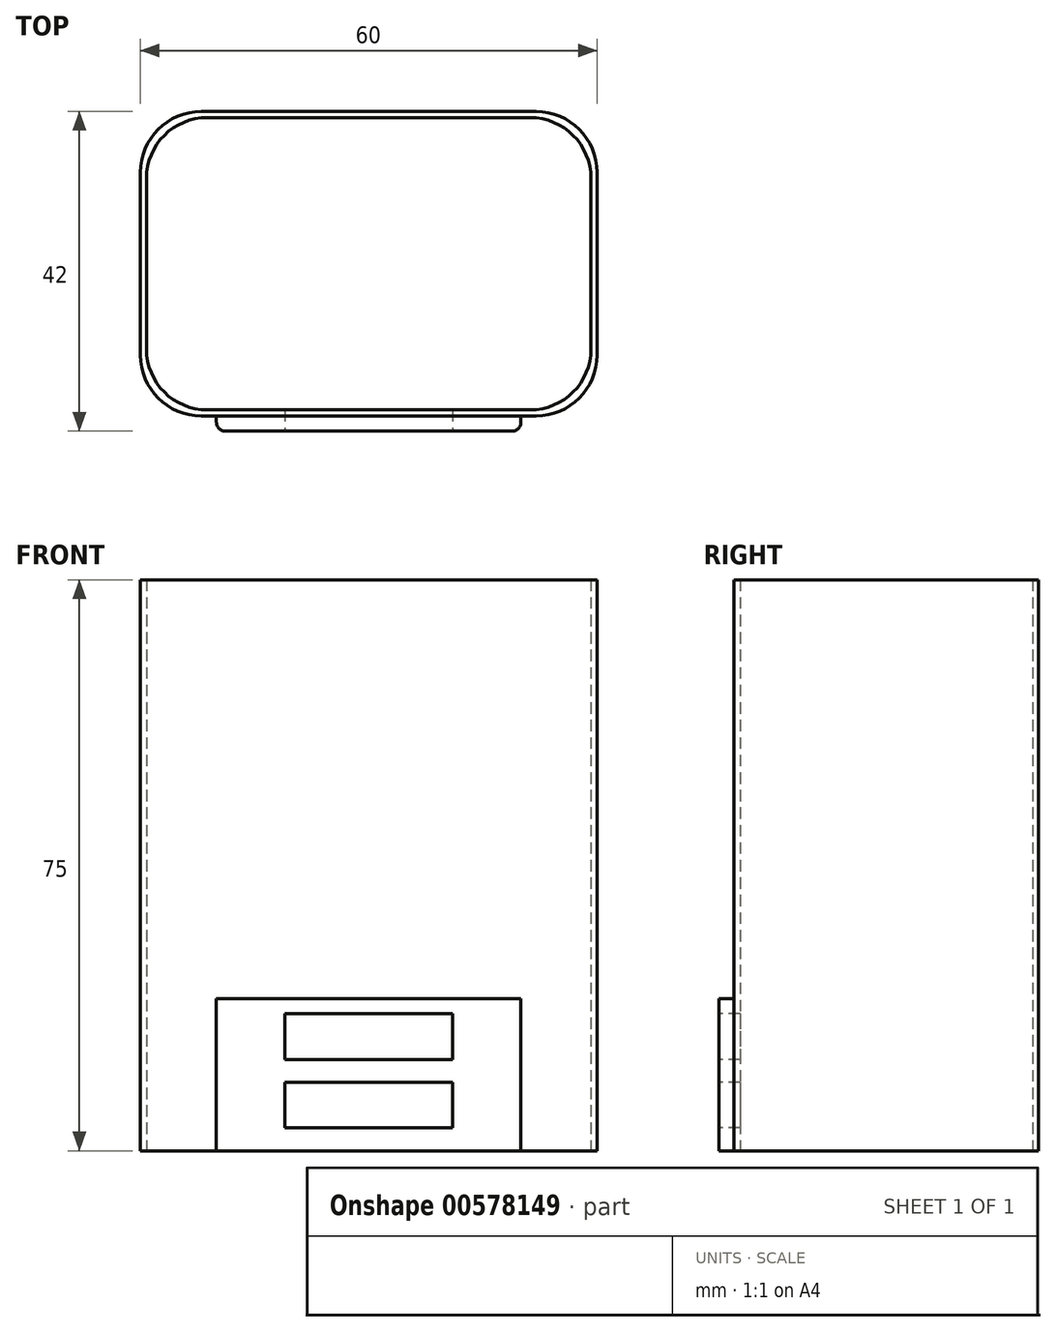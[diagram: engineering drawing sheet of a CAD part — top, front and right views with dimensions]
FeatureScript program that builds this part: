
annotation { "Feature Type Name" : "Feature", "Feature Type Description" : "" }
export const myFeature = defineFeature(function(context is Context, id is Id, definition is map)
    precondition{}
    {
        {
            var Q0;
            Q0=qCreatedBy(makeId("Top.planeOp"),FACE);
            var sketch = newSketch(context, id + "F0", { "sketchPlane" : qUnion([Q0])});
            skLineSegment(sketch, "E0.bottom", {"start": v(30, -33.61) * mm, "end": v(-30, -33.61) * mm});
            skPoint(sketch, "E0.middle", {"position": v(0, 0) * mm});
            skLineSegment(sketch, "E1.bottom", {"start": v(-30, -33.61) * mm, "end": v(30, -33.61) * mm});
            skLineSegment(sketch, "E1.top", {"start": v(-20, -35.61) * mm, "end": v(20, -35.61) * mm});
            skLineSegment(sketch, "E2.top", {"start": v(-10, -41.75) * mm, "end": v(10, -41.75) * mm});
            skLineSegment(sketch, "E3.top", {"start": v(-10, -47.65) * mm, "end": v(10, -47.65) * mm});
            skPoint(sketch, "E4.start.orphan", {"position": v(30, -38.68) * mm});
            skPoint(sketch, "E5.start.orphan", {"position": v(-30, -38.68) * mm});
            skLineSegment(sketch, "E6", {"start": v(-10, -47.65) * mm, "end": v(-10, -35.61) * mm});
            skLineSegment(sketch, "E7", {"start": v(10, -47.65) * mm, "end": v(10, -35.61) * mm});
            skPoint(sketch, "E8.start.orphan", {"position": v(10, -51.4) * mm});
            skPoint(sketch, "E9.start.orphan", {"position": v(-10, -50.9) * mm});
            skPoint(sketch, "E10.orphan", {"position": v(-30, -41.75) * mm});
            skPoint(sketch, "E11.orphan", {"position": v(30, -41.75) * mm});
            skLineSegment(sketch, "E12.top", {"start": v(-30, 6.39) * mm, "end": v(30, 6.39) * mm});
            skLineSegment(sketch, "E12.left", {"start": v(-30, -33.61) * mm, "end": v(-30, 6.39) * mm});
            skLineSegment(sketch, "E12.right", {"start": v(30, -33.61) * mm, "end": v(30, 6.39) * mm});
            skLineSegment(sketch, "E13", {"start": v(20, -35.61) * mm, "end": v(20, -33.61) * mm});
            skLineSegment(sketch, "E14", {"start": v(-20, -35.61) * mm, "end": v(-20, -33.61) * mm});
            skPoint(sketch, "E15.orphan", {"position": v(-30, -35.61) * mm});
            skPoint(sketch, "E16.orphan", {"position": v(30, -35.61) * mm});
            skLineSegment(sketch, "E17.bottom", {"start": v(-29.2, -32.81) * mm, "end": v(29.2, -32.81) * mm});
            skLineSegment(sketch, "E17.top", {"start": v(-29.2, 5.59) * mm, "end": v(29.2, 5.59) * mm});
            skLineSegment(sketch, "E17.left", {"start": v(-29.2, -32.81) * mm, "end": v(-29.2, 5.59) * mm});
            skLineSegment(sketch, "E17.right", {"start": v(29.2, -32.81) * mm, "end": v(29.2, 5.59) * mm});
            skPoint(sketch, "E17.middle", {"position": v(0, -13.61) * mm});
            skSolve(sketch);
        }
        {
            var Q0;
            {var subQ0=sQuery(id+"F0.wireOp",EDGE,"E13");Q0=makeQuery(id+"F0.imprint","IMPRINT",FACE,{"disambiguationData":[TD([[makeQuery(id+"F0.imprint","IMPRINT",EDGE,{"derivedFrom":subQ0}),1.0]])]});}
            extrude(context, id + "F1", {"entities" : qUnion([Q0]), "depth" : 20 * mm, "offsetDistance" : 25 * mm});
        }
        {
            var Q0;
            Q0=makeQuery(id+"F0.imprint","IMPRINT",FACE,{"disambiguationData":[TD([[makeQuery(id+"F0.imprint","IMPRINT",EDGE,{"derivedFrom":sQuery(id+"F0.wireOp",EDGE,"E12.top")}),-1.0]])]});
            extrude(context, id + "F2", {"entities" : qUnion([Q0]), "operationType" : NewBodyOperationType.ADD, "depth" : 75 * mm, "offsetDistance" : 25 * mm});
        }
        {
            var Q0;
            Q0=makeQuery(id+"F1.opExtrude","SWEPT_EDGE",EDGE,{"disambiguationData":[OSD([sQuery(id+"F0.wireOp",EDGE,"E3.top"),sQuery(id+"F0.wireOp",EDGE,"E7")])]});
            var Q1;
            Q1=makeQuery(id+"F1.opExtrude","SWEPT_EDGE",EDGE,{"disambiguationData":[OSD([sQuery(id+"F0.wireOp",EDGE,"E3.top"),sQuery(id+"F0.wireOp",EDGE,"E6")])]});
            var Q2;
            Q2=makeQuery(id+"F1.opExtrude","SWEPT_EDGE",EDGE,{"disambiguationData":[OSD([sQuery(id+"F0.wireOp",EDGE,"E1.top"),sQuery(id+"F0.wireOp",EDGE,"E13")])]});
            var Q3;
            Q3=makeQuery(id+"F1.opExtrude","SWEPT_EDGE",EDGE,{"disambiguationData":[OSD([sQuery(id+"F0.wireOp",EDGE,"E1.top"),sQuery(id+"F0.wireOp",EDGE,"E14")])]});
            var Q4;
            Q4=makeQuery(id+"F1.opExtrude","CAP_FACE",FACE,{"disambiguationData":[OSD([sQuery(id+"F0.wireOp",EDGE,"E2.top"),sQuery(id+"F0.wireOp",EDGE,"E3.top"),sQuery(id+"F0.wireOp",EDGE,"E6"),sQuery(id+"F0.wireOp",EDGE,"E7")])],"isStart":false});
            var Q5;
            Q5=makeQuery(id+"F1.opExtrude","CAP_EDGE",EDGE,{"disambiguationData":[OSD([sQuery(id+"F0.wireOp",EDGE,"E3.top")])],"isStart":true});
            fillet(context, id + "F3", {"entities" : qUnion([Q0, Q1, Q2, Q3, Q4, Q5]), "radius" : 1.2 * mm, "tangentPropagation" : true, "allowEdgeOverflow" : false});
        }
        {
            var Q0;
            Q0=makeQuery(id+"F2.opExtrude","SWEPT_EDGE",EDGE,{"disambiguationData":[OSD([sQuery(id+"F0.wireOp",EDGE,"E17.top"),sQuery(id+"F0.wireOp",EDGE,"E17.right")])]});
            var Q1;
            Q1=makeQuery(id+"F2.opExtrude","SWEPT_EDGE",EDGE,{"disambiguationData":[OSD([sQuery(id+"F0.wireOp",EDGE,"E17.bottom"),sQuery(id+"F0.wireOp",EDGE,"E17.right")])]});
            var Q2;
            Q2=makeQuery(id+"F2.opExtrude","SWEPT_EDGE",EDGE,{"disambiguationData":[OSD([sQuery(id+"F0.wireOp",EDGE,"E17.bottom"),sQuery(id+"F0.wireOp",EDGE,"E17.left")])]});
            var Q3;
            Q3=makeQuery(id+"F2.opExtrude","SWEPT_EDGE",EDGE,{"disambiguationData":[OSD([sQuery(id+"F0.wireOp",EDGE,"E17.top"),sQuery(id+"F0.wireOp",EDGE,"E17.left")])]});
            var Q4;
            Q4=makeQuery(id+"F2.opExtrude","SWEPT_EDGE",EDGE,{"disambiguationData":[OSD([sQuery(id+"F0.wireOp",EDGE,"E1.bottom"),sQuery(id+"F0.wireOp",EDGE,"E12.left")])]});
            var Q5;
            Q5=makeQuery(id+"F2.opExtrude","SWEPT_EDGE",EDGE,{"disambiguationData":[OSD([sQuery(id+"F0.wireOp",EDGE,"E12.top"),sQuery(id+"F0.wireOp",EDGE,"E12.left")])]});
            var Q6;
            Q6=makeQuery(id+"F2.opExtrude","SWEPT_EDGE",EDGE,{"disambiguationData":[OSD([sQuery(id+"F0.wireOp",EDGE,"E1.bottom"),sQuery(id+"F0.wireOp",EDGE,"E12.right")])]});
            var Q7;
            Q7=makeQuery(id+"F2.opExtrude","SWEPT_EDGE",EDGE,{"disambiguationData":[OSD([sQuery(id+"F0.wireOp",EDGE,"E12.top"),sQuery(id+"F0.wireOp",EDGE,"E12.right")])]});
            fillet(context, id + "F4", {"entities" : qUnion([Q0, Q1, Q2, Q3, Q4, Q5, Q6, Q7]), "radius" : 8 * mm, "tangentPropagation" : true, "allowEdgeOverflow" : false});
        }
        {
            var Q0;
            Q0=makeQuery(id+"F1.opExtrude","SWEPT_FACE",FACE,{"disambiguationData":[OSD([sQuery(id+"F0.wireOp",EDGE,"E1.top")])]});
            var sketch = newSketch(context, id + "F5", { "sketchPlane" : qUnion([Q0])});
            skLineSegment(sketch, "E18.bottom", {"start": v(11, 12) * mm, "end": v(-11, 12) * mm});
            skLineSegment(sketch, "E18.top", {"start": v(11, 18) * mm, "end": v(-11, 18) * mm});
            skLineSegment(sketch, "E18.left", {"start": v(11, 12) * mm, "end": v(11, 18) * mm});
            skLineSegment(sketch, "E18.right", {"start": v(-11, 12) * mm, "end": v(-11, 18) * mm});
            skPoint(sketch, "E18.middle", {"position": v(0, 15) * mm});
            skPoint(sketch, "E19.orphan", {"position": v(0, 20) * mm});
            skLineSegment(sketch, "E20.0.1.0", {"start": v(-11, 3) * mm, "end": v(-11, 9) * mm});
            skPoint(sketch, "E20.0.1.1", {"position": v(0, 6) * mm});
            skLineSegment(sketch, "E20.0.1.2", {"start": v(11, 3) * mm, "end": v(11, 9) * mm});
            skLineSegment(sketch, "E20.0.1.3", {"start": v(11, 3) * mm, "end": v(-11, 3) * mm});
            skLineSegment(sketch, "E20.0.1.4", {"start": v(11, 9) * mm, "end": v(-11, 9) * mm});
            skLineSegment(sketch, "E20.direction1", {"start": v(-11, 12) * mm, "end": v(14, 12) * mm, "construction": true});
            skLineSegment(sketch, "E20.direction2", {"start": v(-11, 12) * mm, "end": v(-11, 3) * mm, "construction": true});
            skSolve(sketch);
        }
        {
            var Q0;
            Q0=makeQuery(id+"F5.imprint","IMPRINT",FACE,{"disambiguationData":[TD([[makeQuery(id+"F5.imprint","IMPRINT",EDGE,{"derivedFrom":sQuery(id+"F5.wireOp",EDGE,"E18.bottom")}),-1.0]])]});
            var Q1;
            Q1=makeQuery(id+"F5.imprint","IMPRINT",FACE,{"disambiguationData":[TD([[makeQuery(id+"F5.imprint","IMPRINT",EDGE,{"derivedFrom":sQuery(id+"F5.wireOp",EDGE,"E20.0.1.0")}),-1.0]])]});
            extrude(context, id + "F6", {"entities" : qUnion([Q0, Q1]), "operationType" : NewBodyOperationType.REMOVE, "oppositeDirection" : true, "depth" : 3 * mm, "offsetDistance" : 25 * mm});
        }
    });
